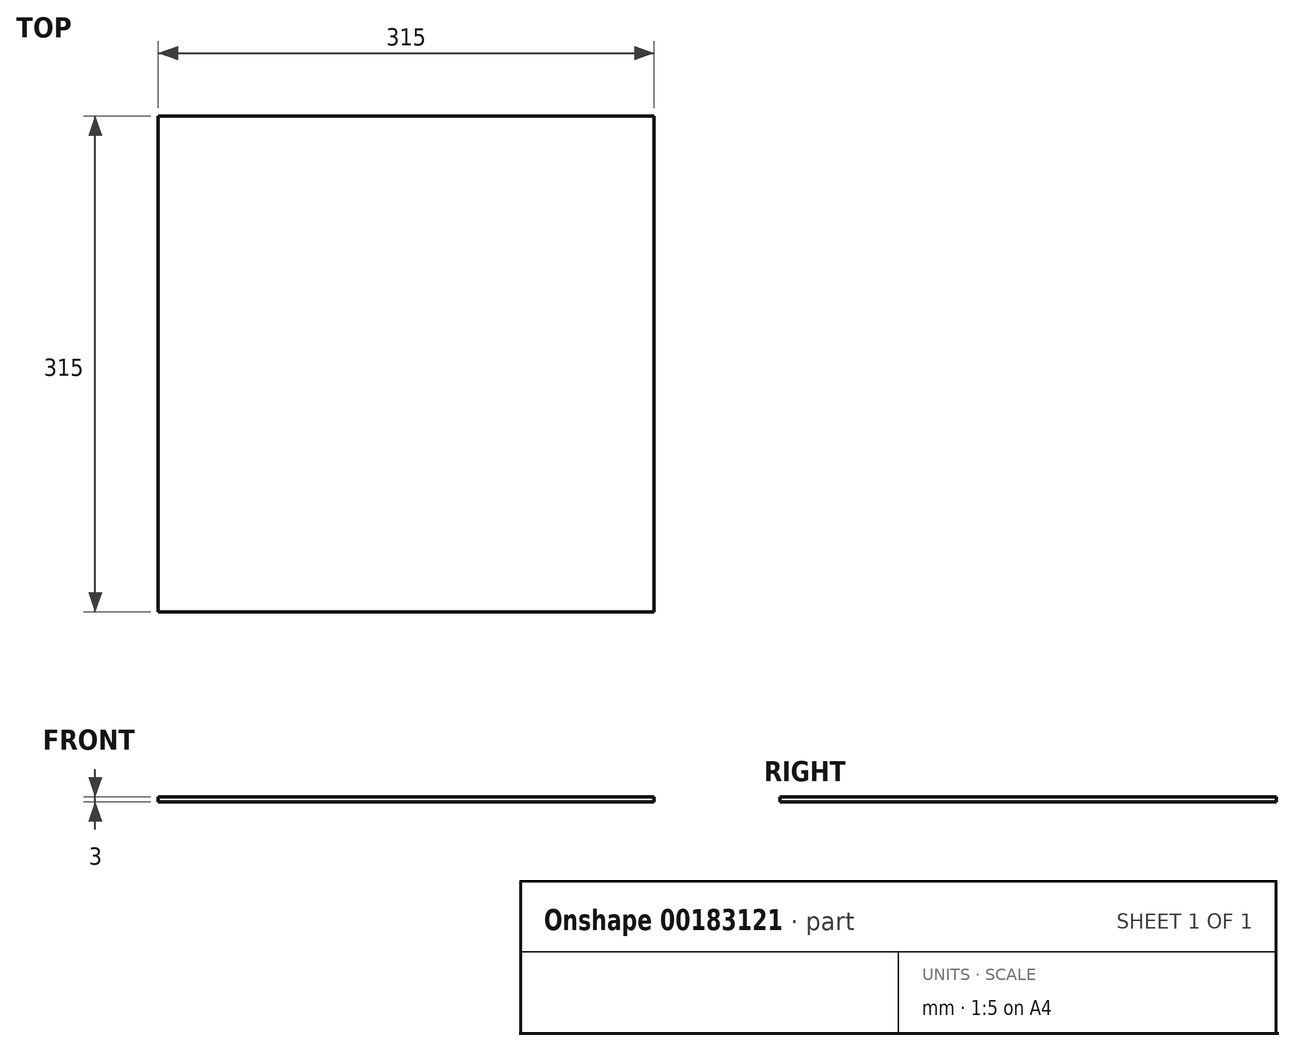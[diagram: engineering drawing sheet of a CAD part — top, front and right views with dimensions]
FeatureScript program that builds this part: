
annotation { "Feature Type Name" : "Feature", "Feature Type Description" : "" }
export const myFeature = defineFeature(function(context is Context, id is Id, definition is map)
    precondition{}
    {
        {
            var Q0;
            Q0=qCreatedBy(makeId("Top.planeOp"),FACE);
            var sketch = newSketch(context, id + "F0", { "sketchPlane" : qUnion([Q0])});
            skLineSegment(sketch, "E0.bottom", {"start": v(-157.5, -157.5) * mm, "end": v(157.5, -157.5) * mm});
            skLineSegment(sketch, "E0.top", {"start": v(-157.5, 157.5) * mm, "end": v(157.5, 157.5) * mm});
            skLineSegment(sketch, "E0.left", {"start": v(-157.5, -157.5) * mm, "end": v(-157.5, 157.5) * mm});
            skLineSegment(sketch, "E0.right", {"start": v(157.5, -157.5) * mm, "end": v(157.5, 157.5) * mm});
            skPoint(sketch, "E0.middle", {"position": v(0, 0) * mm});
            skSolve(sketch);
        }
        {
            var Q0;
            Q0=makeQuery(id+"F0.imprint","IMPRINT",FACE,{"disambiguationData":[TD([[makeQuery(id+"F0.imprint","IMPRINT",EDGE,{"derivedFrom":sQuery(id+"F0.wireOp",EDGE,"E0.bottom")}),1.0]])]});
            extrude(context, id + "F1", {"entities" : qUnion([Q0]), "depth" : 3 * mm});
        }
    });
